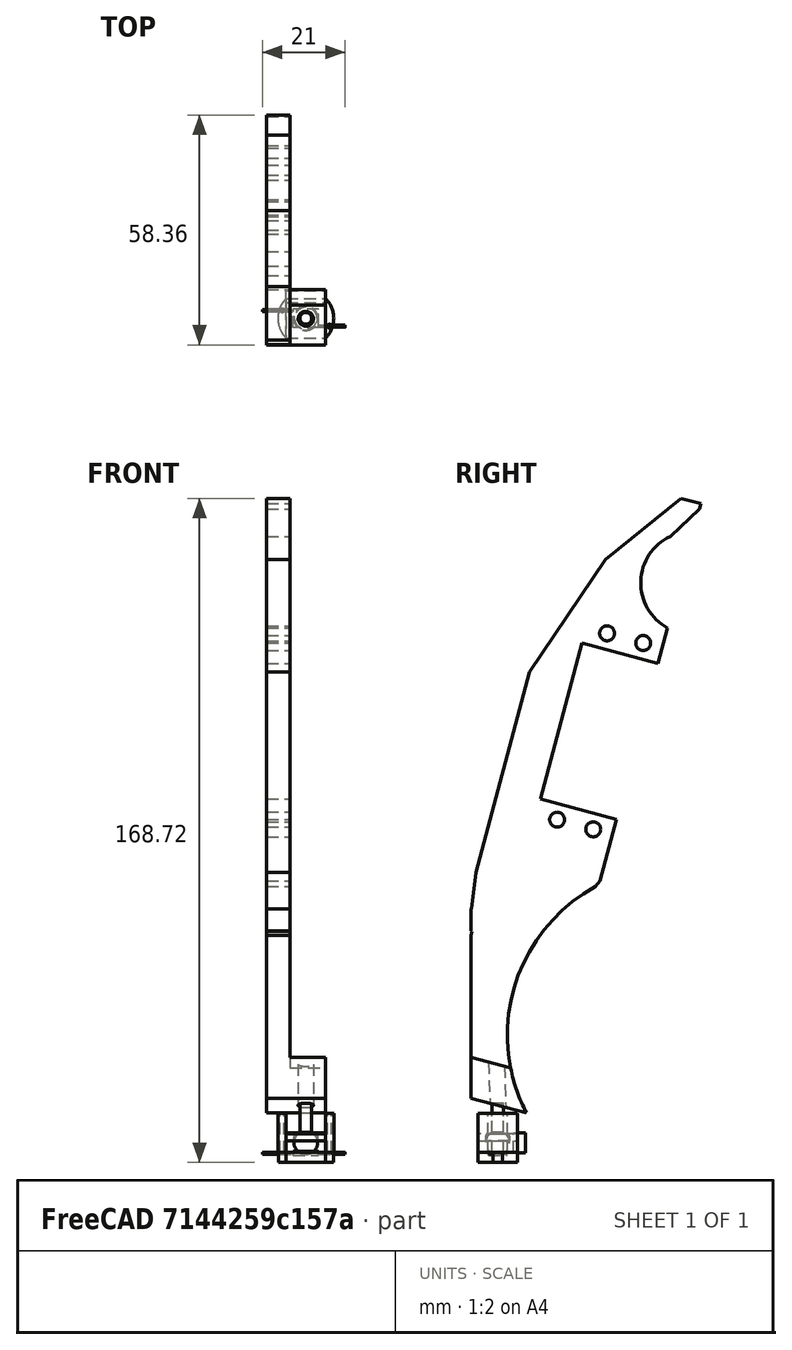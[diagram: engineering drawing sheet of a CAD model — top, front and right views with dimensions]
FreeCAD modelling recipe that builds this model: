
FCSTD DOCUMENT  (FreeCAD 0.16R6703 (Git))
Label: Feet sensor and leg 0.1
License: All rights reserved
LicenseURL: http://en.wikipedia.org/wiki/All_rights_reserved
objects: Part::Cut×29, Part::Box×23, Part::Cylinder×19, Part::Fuse×8, Part::MultiCommon×3, Part::Sphere×2, Part::Chamfer×2
note: 86 computed .brp shape members not serialized (recipe doc carries the construction recipe); baked Part::Feature solids carry a one-line shape summary decoded from their .brp

FEATURE [Part::Sphere] Sphere
  Angle1 = -90
  Angle2 = 90
  Angle3 = 360
  Radius = 3
FEATURE [Part::Cylinder] Cylinder
  Angle = 360
  Height = 10
  Radius = 1.5
FEATURE [Part::Box] Box  label="Cube"
  Height = 1
  Length = 6.5
  Placement = pos=(-3.25,-2.4,-4.2) rot=(0,0,1;0rad)
  Width = 4.8
FEATURE [Part::Cylinder] Cylinder001
  Angle = 360
  Height = 10
  Placement = pos=(-11,2,-3.7) rot=(0,1,0;1.5708rad)
  Radius = 0.25
FEATURE [Part::Cylinder] Cylinder002
  Angle = 360
  Height = 10
  Placement = pos=(0,-2,-3.7) rot=(0,1,0;1.5708rad)
  Radius = 0.25
FEATURE [Part::Box] Box001  label="Cube001"
  Height = 7.25
  Length = 14
  Placement = pos=(-7,-5,-6) rot=(0,0,1;0rad)
  Width = 10
FEATURE [Part::Box] Box002  label="Cube002"
  Height = 1
  Length = 6.5
  Placement = pos=(-3.25,-2.4,-4.2) rot=(0,0,1;0rad)
  Width = 4.8
FEATURE [Part::Cylinder] Cylinder003
  Angle = 360
  Height = 10
  Placement = pos=(-11,2,-3.7) rot=(0,1,0;1.5708rad)
  Radius = 0.25
FEATURE [Part::Cylinder] Cylinder004
  Angle = 360
  Height = 10
  Placement = pos=(0,-2,-3.7) rot=(0,1,0;1.5708rad)
  Radius = 0.25
FEATURE [Part::Fuse] Fusion
  Base = -> Cylinder003
  Tool = -> Cylinder004
FEATURE [Part::Fuse] Fusion001
  Base = -> Box002
  Tool = -> Fusion
FEATURE [Part::Box] Box003  label="Cube003"
  Height = 3
  Length = 10
  Placement = pos=(-5,-6,-3.5) rot=(0,0,1;0rad)
  Width = 12
FEATURE [Part::Cut] Cut
  Base = -> Box001
  Tool = -> Box003
FEATURE [Part::Cut] Cut001
  Base = -> Cut
  Tool = -> Fusion001
FEATURE [Part::Fuse] Fusion002
  Base = -> Cylinder001
  Tool = -> Cylinder002
FEATURE [Part::Fuse] Fusion003  label="Switch"
  Base = -> Box
  Tool = -> Fusion002
FEATURE [Part::Box] Box004  label="Cube004"
  Height = 5
  Length = 10
  Placement = pos=(-5,4,-3.55) rot=(0,0,1;0rad)
  Width = 3
FEATURE [Part::Sphere] Sphere001
  Angle1 = -90
  Angle2 = 90
  Angle3 = 360
  Radius = 3.1
FEATURE [Part::Cylinder] Cylinder005
  Angle = 360
  Height = 10
  Placement = pos=(0,0,0.5) rot=(0,0,1;0rad)
  Radius = 2.5
FEATURE [Part::Fuse] Fusion004
  Base = -> Sphere001
  Tool = -> Cylinder005
FEATURE [Part::Cut] Cut002
  Base = -> Cut001
  Tool = -> Fusion004
FEATURE [Part::Fuse] Fusion005  label="Ball and Screw"
  Base = -> Sphere
  Placement = pos=(0,0,-1) rot=(0,0,1;0rad)
  Tool = -> Cylinder
FEATURE [Part::Cut] Cut003
  Base = -> Cut001
  Tool = -> Fusion004
FEATURE [Part::Box] Box005  label="Cube005"
  Height = 8
  Length = 21
  Placement = pos=(-9,-7,-3.5) rot=(0,0,1;0rad)
  Width = 17
FEATURE [Part::Box] Box006  label="Cube006"
  Height = 12
  Length = 21
  Placement = pos=(-9,-7,-3.5) rot=(0,0,1;0rad)
  Width = 17
FEATURE [Part::Cut] Cut004  label="Bottom Switch holder"
  Base = -> Cut003
  Tool = -> Box005
FEATURE [Part::MultiCommon] Common  label="Ball and screw holder"
  Shapes = -> [Cut002,Box006]
FEATURE [Part::Cylinder] Cylinder006
  Angle = 360
  Height = 10
  Placement = pos=(0,0,-3.5) rot=(0,0,1;0rad)
  Radius = 7.1
FEATURE [Part::Box] Box007  label="Cube007"
  Height = 10
  Length = 10
  Placement = pos=(-5,-9,-3.5) rot=(0,0,1;0rad)
  Width = 20
FEATURE [Part::Cut] Cut005
  Base = -> Cylinder006
  Tool = -> Box007
FEATURE [Part::Cylinder] Cylinder007
  Angle = 360
  Height = 10
  Placement = pos=(0,0,-3.5) rot=(0,0,1;0rad)
  Radius = 7.1
FEATURE [Part::MultiCommon] Common001
  Shapes = -> [Common,Cylinder007]
FEATURE [Part::Fuse] Fusion006
  Base = -> Cut005
  Tool = -> Common001
FEATURE [Part::Cylinder] Cylinder008
  Angle = 360
  Height = 10
  Placement = pos=(0,0,-6.5) rot=(0,0,1;0rad)
  Radius = 7.1
FEATURE [Part::MultiCommon] Common002
  Shapes = -> [Cut004,Cylinder008]
FEATURE [Part::Cylinder] Cylinder009
  Angle = 360
  Height = 13
  Placement = pos=(-6,2,-4) rot=(0,0,1;0rad)
  Radius = 0.5
FEATURE [Part::Cut] Cut006
  Base = -> Fusion006
  Tool = -> Cylinder009
FEATURE [Part::Cylinder] Cylinder010
  Angle = 360
  Height = 13
  Placement = pos=(6,-2,-4) rot=(0,0,1;0rad)
  Radius = 0.5
FEATURE [Part::Cut] Cut007
  Base = -> Cut006
  Tool = -> Cylinder010
FEATURE [Part::Box] Box008  label="Cube008"
  Height = 12
  Length = 41
  Placement = pos=(42,14,-1) rot=(0,0,1;0rad)
  Width = 20
FEATURE [Part::Cylinder] Cylinder011
  Angle = 360
  Height = 12
  Placement = pos=(38,19.5,-1) rot=(0,0,1;0rad)
  Radius = 1.9
FEATURE [Part::Cylinder] Cylinder012
  Angle = 360
  Height = 12
  Placement = pos=(38,29,-1) rot=(0,0,1;0rad)
  Radius = 1.9
FEATURE [Part::Cylinder] Cylinder013
  Angle = 360
  Height = 12
  Placement = pos=(87,29,-1) rot=(0,0,1;0rad)
  Radius = 1.9
FEATURE [Part::Cylinder] Cylinder014
  Angle = 360
  Height = 12
  Placement = pos=(87,19.5,-1) rot=(0,0,1;0rad)
  Radius = 1.9
FEATURE [Part::Box] Box009  label="Cube009"
  Height = 6
  Length = 184
  Width = 34
FEATURE [Part::Box] Box010  label="Cube010"
  Height = 12
  Length = 37
  Width = 8
FEATURE [Part::Cylinder] Cylinder015
  Angle = 360
  Height = 10
  Placement = pos=(20,37,0) rot=(0,0,1;0rad)
  Radius = 13
FEATURE [Part::Cut] Cut008
  Base = -> Box009
  Tool = -> Box010
FEATURE [Part::Cut] Cut009
  Base = -> Cut008
  Tool = -> Cylinder015
FEATURE [Part::Cylinder] Cylinder016
  Angle = 360
  Height = 10
  Placement = pos=(132,63,0) rot=(0,0,1;0rad)
  Radius = 43
FEATURE [Part::Cut] Cut010
  Base = -> Cut009
  Tool = -> Cylinder016
FEATURE [Part::Box] Box011  label="Cube011"
  Height = 10
  Length = 41
  Placement = pos=(120,0,0) rot=(0,0,1;0rad)
  Width = 6
FEATURE [Part::Cut] Cut011
  Base = -> Cut010
  Tool = -> Box011
FEATURE [Part::Box] Box012  label="Cube012"
  Height = 10
  Length = 23
  Placement = pos=(161,0,0) rot=(0,0,1;0rad)
  Width = 17
FEATURE [Part::Cut] Cut012
  Base = -> Cut011
  Tool = -> Box012
FEATURE [Part::Box] Box013  label="Cube013"
  Height = 10
  Length = 13
  Placement = pos=(0,8,0) rot=(0,0,1;0rad)
  Width = 11
FEATURE [Part::Cut] Cut013
  Base = -> Cut012
  Tool = -> Box013
FEATURE [Part::Box] Box014  label="Cube014"
  Height = 10
  Length = 53
  Placement = pos=(-16,28,0) rot=(0,0,-1;0.628319rad)
  Width = 10
FEATURE [Part::Cut] Cut014
  Base = -> Cut013
  Tool = -> Box014
FEATURE [Part::Box] Box015  label="Cube015"
  Height = 10
  Length = 49
  Placement = pos=(16,5,0) rot=(0,0,-1;0.331613rad)
  Width = 10
FEATURE [Part::Cut] Cut015
  Base = -> Cut014
  Tool = -> Box015
FEATURE [Part::Box] Box016  label="Cube016"
  Height = 10
  Length = 76
  Placement = pos=(46,-7,0) rot=(0,0,1;0rad)
  Width = 10
FEATURE [Part::Cut] Cut016
  Base = -> Cut015
  Tool = -> Box016
FEATURE [Part::Box] Box017  label="Cube017"
  Height = 10
  Length = 65
  Placement = pos=(115,-7,0) rot=(0,0,1;0.261799rad)
  Width = 11
FEATURE [Part::Cut] Cut017
  Base = -> Cut016
  Tool = -> Box017
FEATURE [Part::Box] Box018  label="Cube018"
  Height = 10
  Length = 14
  Placement = pos=(174,10,0) rot=(0,0,1;0.279253rad)
  Width = 10
FEATURE [Part::Cut] Cut018
  Base = -> Cut017
  Tool = -> Box018
FEATURE [Part::Box] Box019  label="Cube019"
  Height = 10
  Length = 10
  Placement = pos=(106,-7,0) rot=(0,0,1;0.139626rad)
  Width = 10
FEATURE [Part::Cut] Cut019
  Base = -> Cut018
  Tool = -> Box019
FEATURE [Part::Cut] Cut020
  Base = -> Cut019
  Tool = -> Box008
FEATURE [Part::Cut] Cut021
  Base = -> Cut020
  Tool = -> Cylinder014
FEATURE [Part::Cut] Cut022
  Base = -> Cut021
  Tool = -> Cylinder013
FEATURE [Part::Cut] Cut023
  Base = -> Cut022
  Tool = -> Cylinder012
FEATURE [Part::Cut] Cut024
  Base = -> Cut023
  Tool = -> Cylinder011
FEATURE [Part::Chamfer] Chamfer
  Base = -> Cut024
  Edges = 1 edges r=6: [Edge36]
FEATURE [Part::Chamfer] Chamfer001
  Base = -> Chamfer
  Edges = 1 edges r=1: [Edge59]
FEATURE [Part::Box] Box020  label="Cube020"
  Height = 10
  Length = 10
  Placement = pos=(151,12,5) rot=(0,0,1;0rad)
  Width = 21
FEATURE [Part::Box] Box021  label="Cube021"
  Height = 13
  Length = 26
  Placement = pos=(161,15,-3) rot=(0,0,1;0rad)
  Width = 23
FEATURE [Part::Cut] Cut025
  Base = -> Chamfer001
  Tool = -> Box021
FEATURE [Part::Cylinder] Cylinder017
  Angle = 360
  Height = 19
  Placement = pos=(132,63,0) rot=(0,0,1;0rad)
  Radius = 43
FEATURE [Part::Cut] Cut026
  Base = -> Box020
  Tool = -> Cylinder017
FEATURE [Part::Box] Box022  label="Cube022"
  Height = 20
  Length = 65
  Placement = pos=(115,-7,0) rot=(0,0,1;0.261799rad)
  Width = 11
FEATURE [Part::Cut] Cut027
  Base = -> Cut026
  Tool = -> Box022
FEATURE [Part::Cylinder] Cylinder018
  Angle = 360
  Height = 18
  Placement = pos=(146.076,19.1828,10) rot=(-0.146221,0.978386,0.146221;1.59265rad)
  Radius = 2
FEATURE [Part::Cut] Cut028
  Base = -> Cut027
  Tool = -> Cylinder018
FEATURE [Part::Fuse] Fusion007
  Base = -> Cut025
  Placement = pos=(-10,18.7829,170.16) rot=(-0.129428,0.983106,-0.129428;1.58783rad)
  Tool = -> Cut028
